annotation { "Feature Type Name" : "Feature", "Feature Type Description" : "" }
export const myFeature = defineFeature(function(context is Context, id is Id, definition is map)
    precondition{}
    {
        {
            var Q0;
            Q0=qCreatedBy(makeId("Top.planeOp"),FACE);
            var sketch = newSketch(context, id + "F0", { "sketchPlane" : qUnion([Q0])});
            skLineSegment(sketch, "E0.bottom", {"start": v(30, 40) * mm, "end": v(-30, 40) * mm});
            skLineSegment(sketch, "E0.top", {"start": v(30, -40) * mm, "end": v(-30, -40) * mm});
            skLineSegment(sketch, "E0.left", {"start": v(40, 30) * mm, "end": v(40, -30) * mm});
            skLineSegment(sketch, "E0.right", {"start": v(-40, 30) * mm, "end": v(-40, -30) * mm});
            skLineSegment(sketch, "E1.bottom", {"start": v(-29.2, 39.2) * mm, "end": v(29.2, 39.2) * mm});
            skLineSegment(sketch, "E1.top", {"start": v(-29.2, -39.2) * mm, "end": v(29.2, -39.2) * mm});
            skLineSegment(sketch, "E1.left", {"start": v(-39.2, 29.2) * mm, "end": v(-39.2, -29.2) * mm});
            skLineSegment(sketch, "E1.right", {"start": v(39.2, 29.2) * mm, "end": v(39.2, -29.2) * mm});
            skPoint(sketch, "E2.visualSharp", {"position": v(-39.2, 39.2) * mm});
            skArc(sketch, "E2.filletArc", {"start": v(-29.2, 39.2) * mm, "mid": v(-36.27, 36.27) * mm, "end": v(-39.2, 29.2) * mm});
            skPoint(sketch, "E3.visualSharp", {"position": v(39.2, 39.2) * mm});
            skArc(sketch, "E3.filletArc", {"start": v(39.2, 29.2) * mm, "mid": v(36.27, 36.27) * mm, "end": v(29.2, 39.2) * mm});
            skPoint(sketch, "E4.visualSharp", {"position": v(-40, 40) * mm});
            skArc(sketch, "E4.filletArc", {"start": v(-30, 40) * mm, "mid": v(-37.07, 37.07) * mm, "end": v(-40, 30) * mm});
            skPoint(sketch, "E5.visualSharp", {"position": v(-39.2, -39.2) * mm});
            skArc(sketch, "E5.filletArc", {"start": v(-39.2, -29.2) * mm, "mid": v(-36.27, -36.27) * mm, "end": v(-29.2, -39.2) * mm});
            skPoint(sketch, "E6.visualSharp", {"position": v(-40, -40) * mm});
            skArc(sketch, "E6.filletArc", {"start": v(-40, -30) * mm, "mid": v(-37.07, -37.07) * mm, "end": v(-30, -40) * mm});
            skPoint(sketch, "E7.visualSharp", {"position": v(39.2, -39.2) * mm});
            skArc(sketch, "E7.filletArc", {"start": v(29.2, -39.2) * mm, "mid": v(36.27, -36.27) * mm, "end": v(39.2, -29.2) * mm});
            skPoint(sketch, "E8.visualSharp", {"position": v(40, -40) * mm});
            skArc(sketch, "E8.filletArc", {"start": v(30, -40) * mm, "mid": v(37.07, -37.07) * mm, "end": v(40, -30) * mm});
            skPoint(sketch, "E9.visualSharp", {"position": v(40, 40) * mm});
            skArc(sketch, "E9.filletArc", {"start": v(40, 30) * mm, "mid": v(37.07, 37.07) * mm, "end": v(30, 40) * mm});
            skSolve(sketch);
        }
        {
            var Q0;
            Q0=makeQuery(id+"F0.imprint","IMPRINT",FACE,{"disambiguationData":[TD([[makeQuery(id+"F0.imprint","IMPRINT",EDGE,{"derivedFrom":sQuery(id+"F0.wireOp",EDGE,"E0.bottom")}),1.0]])]});
            var Q1;
            Q1=makeQuery(id+"F0.imprint","IMPRINT",FACE,{"disambiguationData":[TD([[makeQuery(id+"F0.imprint","IMPRINT",EDGE,{"derivedFrom":sQuery(id+"F0.wireOp",EDGE,"E1.bottom")}),-1.0]])]});
            extrude(context, id + "F1", {"entities" : qUnion([Q0, Q1]), "depth" : 1 * mm, "offsetDistance" : 25 * mm});
        }
        {
            var Q0;
            Q0=makeQuery(id+"F0.imprint","IMPRINT",FACE,{"disambiguationData":[TD([[makeQuery(id+"F0.imprint","IMPRINT",EDGE,{"derivedFrom":sQuery(id+"F0.wireOp",EDGE,"E0.bottom")}),1.0]])]});
            extrude(context, id + "F2", {"entities" : qUnion([Q0]), "operationType" : NewBodyOperationType.ADD, "depth" : 80 * mm, "offsetDistance" : 25 * mm});
        }
        {
            var Q0;
            {var subQ0=sQuery(id+"F0.wireOp",EDGE,"E0.left");Q0=makeQuery(id+"F2.boolean.opBoolean","MERGE",FACE,{"derivedFrom":[makeQuery(id+"F1.opExtrude","SWEPT_FACE",FACE,{"disambiguationData":[OSD([subQ0])]}),makeQuery(id+"F2.opExtrude","SWEPT_FACE",FACE,{"disambiguationData":[OSD([subQ0])]})]});}
            var sketch = newSketch(context, id + "F3", { "sketchPlane" : qUnion([Q0])});
            skLineSegment(sketch, "E10", {"start": v(0, 80) * mm, "end": v(0, 0) * mm, "construction": true});
            skLineSegment(sketch, "E11", {"start": v(-1.56, 36.42) * mm, "end": v(-20.69, 41.56) * mm});
            skLineSegment(sketch, "E12", {"start": v(-20.69, 41.56) * mm, "end": v(-33.86, 50.95) * mm});
            skLineSegment(sketch, "E13", {"start": v(-33.86, 50.95) * mm, "end": v(-30.68, 50.95) * mm});
            skLineSegment(sketch, "E14", {"start": v(-30.68, 50.95) * mm, "end": v(-35.32, 52.9) * mm});
            skLineSegment(sketch, "E15", {"start": v(-35.32, 52.9) * mm, "end": v(-30.68, 52.9) * mm});
            skLineSegment(sketch, "E16", {"start": v(-30.68, 52.9) * mm, "end": v(-36.98, 55.56) * mm});
            skLineSegment(sketch, "E17", {"start": v(-36.98, 55.56) * mm, "end": v(-30.68, 55.56) * mm});
            skLineSegment(sketch, "E18", {"start": v(-30.68, 55.56) * mm, "end": v(-35.32, 57.51) * mm});
            skLineSegment(sketch, "E19", {"start": v(-35.32, 57.51) * mm, "end": v(-30.68, 59.01) * mm});
            skFitSpline(sketch, "E20", {"points": [v(-30.68, 59.01) * mm, v(-29.83, 68.66) * mm, v(-17.62, 80) * mm, v(0, 82.33) * mm], "startDerivative": vector(-3.3, 34.77) * mm, "endDerivative": vector(48.99, -0.34) * mm});
            skFitSpline(sketch, "E21", {"points": [v(-9.8, 46.07) * mm, v(-4.19, 43.14) * mm, v(0, 45.83) * mm, v(0, 45.7) * mm, v(-4.16, 42.86) * mm, v(-10, 45.9) * mm, v(-9.8, 46.07) * mm]});
            skFitSpline(sketch, "E22", {"points": [v(0, 45.7) * mm, v(-3.44, 50.26) * mm, v(0, 51.13) * mm], "startDerivative": vector(-10.06, 9.87) * mm, "endDerivative": vector(10.89, 0.62) * mm});
            skEllipse(sketch, "E23", {"center": v(-12.1, 63.87) * mm, "majorRadius": 9.28 * mm, "minorRadius": 4.23 * mm, "majorAxis": v(0, 1)});
            skCircle(sketch, "E24", {"center": v(-12, 66.11) * mm, "radius": 2.25 * mm});
            skPoint(sketch, "E24.second.point", {"position": v(-13.87, 67.37) * mm});
            skPoint(sketch, "E24.third.point", {"position": v(-10.42, 67.72) * mm});
            skFitSpline(sketch, "E25", {"points": [v(-23.74, 76.21) * mm, v(-31.29, 81.58) * mm, v(-29.4, 93.5) * mm], "startDerivative": vector(-20.78, 8.97) * mm, "endDerivative": vector(8.82, 25.25) * mm});
            skFitSpline(sketch, "E26", {"points": [v(-29.4, 93.5) * mm, v(-19.29, 88.49) * mm, v(-14.16, 81.2) * mm], "startDerivative": vector(21.27, -7.86) * mm, "endDerivative": vector(8.96, -17) * mm});
            skFitSpline(sketch, "E27.MirrorCS", {"points": [v(30.68, 59.01) * mm, v(29.83, 68.66) * mm, v(17.62, 80) * mm, v(0, 82.33) * mm], "startDerivative": vector(3.3, 34.77) * mm, "endDerivative": vector(-48.99, -0.34) * mm});
            skFitSpline(sketch, "E28.MirrorCS", {"points": [v(23.74, 76.21) * mm, v(31.29, 81.58) * mm, v(29.4, 93.5) * mm], "startDerivative": vector(20.78, 8.97) * mm, "endDerivative": vector(-8.82, 25.25) * mm});
            skFitSpline(sketch, "E29.MirrorCS", {"points": [v(29.4, 93.5) * mm, v(19.29, 88.49) * mm, v(14.16, 81.2) * mm], "startDerivative": vector(-21.27, -7.86) * mm, "endDerivative": vector(-8.96, -17) * mm});
            skEllipse(sketch, "E30.MirrorC", {"center": v(12.1, 63.87) * mm, "majorRadius": 9.28 * mm, "minorRadius": 4.23 * mm, "majorAxis": v(0, 1)});
            skCircle(sketch, "E31.MirrorC", {"center": v(12, 66.11) * mm, "radius": 2.25 * mm});
            skFitSpline(sketch, "E32.MirrorC", {"points": [v(9.8, 46.07) * mm, v(4.19, 43.14) * mm, v(0, 45.83) * mm, v(0, 45.7) * mm, v(4.16, 42.86) * mm, v(10, 45.9) * mm, v(9.8, 46.07) * mm]});
            skFitSpline(sketch, "E33.MirrorCS", {"points": [v(0, 45.7) * mm, v(3.44, 50.26) * mm, v(0, 51.13) * mm], "startDerivative": vector(10.06, 9.87) * mm, "endDerivative": vector(-10.89, 0.62) * mm});
            skLineSegment(sketch, "E34.MirrorCS", {"start": v(1.56, 36.42) * mm, "end": v(20.69, 41.56) * mm});
            skLineSegment(sketch, "E35.MirrorCS", {"start": v(20.69, 41.56) * mm, "end": v(33.86, 50.95) * mm});
            skLineSegment(sketch, "E36.MirrorCS", {"start": v(33.86, 50.95) * mm, "end": v(30.68, 50.95) * mm});
            skLineSegment(sketch, "E37.MirrorCS", {"start": v(30.68, 50.95) * mm, "end": v(35.32, 52.9) * mm});
            skLineSegment(sketch, "E38.MirrorCS", {"start": v(35.32, 52.9) * mm, "end": v(30.68, 52.9) * mm});
            skLineSegment(sketch, "E39.MirrorCS", {"start": v(30.68, 52.9) * mm, "end": v(36.98, 55.56) * mm});
            skLineSegment(sketch, "E40.MirrorCS", {"start": v(36.98, 55.56) * mm, "end": v(30.68, 55.56) * mm});
            skLineSegment(sketch, "E41.MirrorCS", {"start": v(30.68, 55.56) * mm, "end": v(35.32, 57.51) * mm});
            skLineSegment(sketch, "E42.MirrorCS", {"start": v(35.32, 57.51) * mm, "end": v(30.68, 59.01) * mm});
            skPoint(sketch, "E43.visualSharp", {"position": v(0, 36) * mm});
            skArc(sketch, "E43.filletArc", {"start": v(-1.56, 36.42) * mm, "mid": v(0, 36.21) * mm, "end": v(1.56, 36.42) * mm});
            skText(sketch, "E44", { "text": "Stephenie", "fontName": "NotoSansCJKsc-Regular.otf"});
            skText(sketch, "E45", { "text": "The Crazy \n", "fontName": "OpenSans-Regular.ttf"});
            skText(sketch, "E46", { "text": "Cat Lady", "fontName": "OpenSans-Regular.ttf"});
            const initialGuessF3  = {"E44": [-0.03, 0.026, 1, 0, 0.00907], "E45": [-0.03, 0.01565, 1, 0, 0.00935], "E46": [-0.03, 0.004, 1, 0, 0.01065]};
            skSetInitialGuess(sketch, initialGuessF3);
            skSolve(sketch);
        }
        {
            var Q0;
            Q0 = qSketchRegion(id + "F3", true);
            var Q1;
            Q1=makeQuery(id+"F3.imprint","IMPRINT",FACE,{"disambiguationData":[TD([[makeQuery(id+"F3.imprint","IMPRINT",EDGE,{"derivedFrom":sQuery(id+"F3.wireOp",EDGE,"E24")}),1.0]])]});
            var Q2;
            Q2=makeQuery(id+"F3.imprint","IMPRINT",FACE,{"disambiguationData":[TD([[makeQuery(id+"F3.imprint","IMPRINT",EDGE,{"derivedFrom":sQuery(id+"F3.wireOp",EDGE,"E31.MirrorC")}),-1.0]])]});
            extrude(context, id + "F4", {"entities" : qUnion([Q0, Q1, Q2]), "endBound" : BoundingType.SYMMETRIC, "depth" : .8 * mm, "offsetDistance" : 25 * mm});
        }
        {
            var Q0;
            {var subQ3=sQuery(id+"F3.wireOp",EDGE,"E21");var subQ5=sQuery(id+"F3.wireOp",EDGE,"E32.MirrorC");var subQ8=makeQuery(id+"F3.imprint","INTERSECT",VERTEX,{"disambiguationData":[OD(0.0)],"derivedFrom":[subQ3,subQ5]});Q0=makeQuery(id+"F3.imprint","IMPRINT",FACE,{"disambiguationData":[TD([[makeQuery(id+"F3.imprint","IMPRINT",EDGE,{"disambiguationData":[TD([[subQ8,1.0]])],"derivedFrom":subQ3}),1.0]])]});}
            extrude(context, id + "F5", {"entities" : qUnion([Q0]), "operationType" : NewBodyOperationType.ADD, "depth" : .8 * mm, "offsetDistance" : 25 * mm});
        }
    });